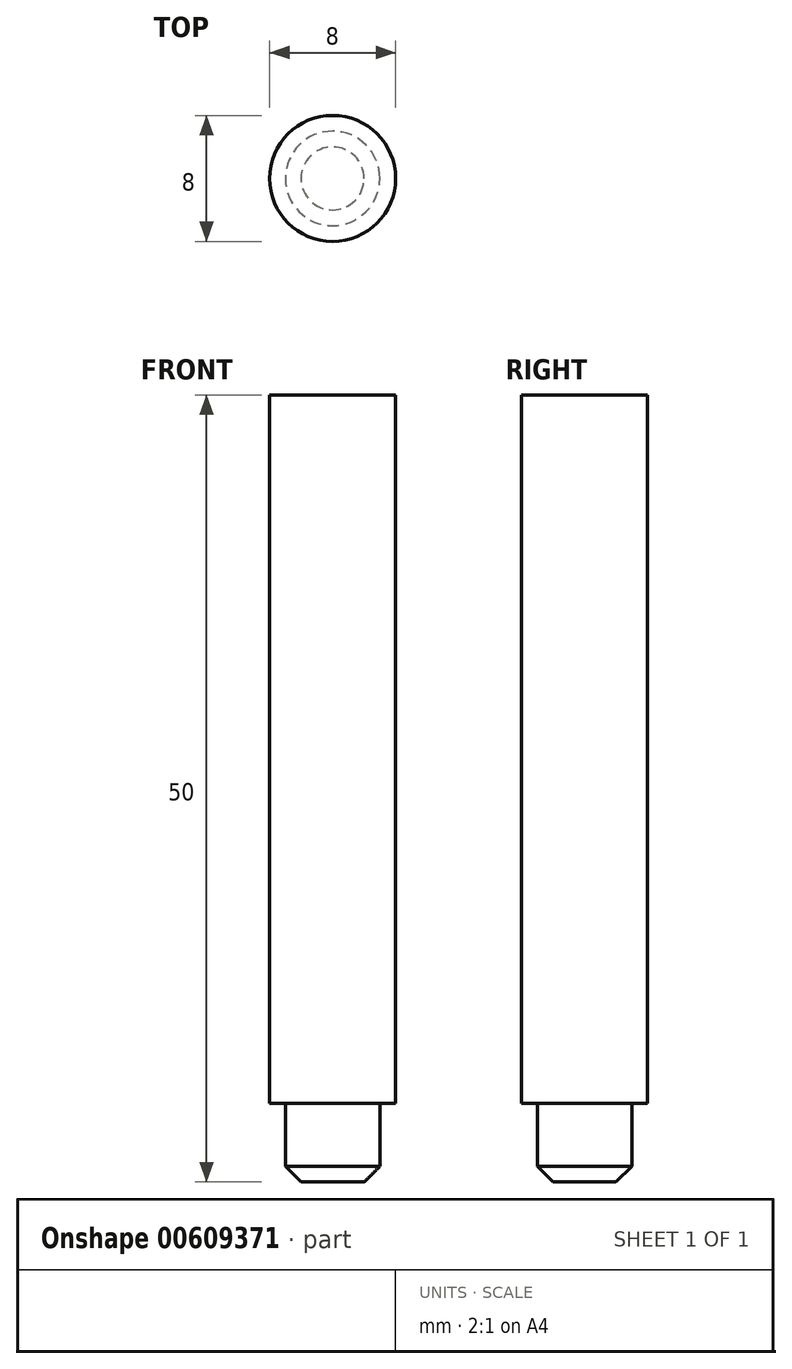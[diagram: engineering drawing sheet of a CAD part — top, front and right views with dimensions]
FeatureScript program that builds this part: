
annotation { "Feature Type Name" : "Feature", "Feature Type Description" : "" }
export const myFeature = defineFeature(function(context is Context, id is Id, definition is map)
    precondition{}
    {
        {
            var Q0;
            Q0=qCreatedBy(makeId("Top.planeOp"),FACE);
            var sketch = newSketch(context, id + "F0", { "sketchPlane" : qUnion([Q0])});
            skCircle(sketch, "E0", {"center": v(0, 0) * mm, "radius": 4 * mm});
            skCircle(sketch, "E1", {"center": v(0, 0) * mm, "radius": 3 * mm});
            skSolve(sketch);
        }
        {
            var Q0;
            Q0=makeQuery(id+"F0.imprint","IMPRINT",FACE,{"disambiguationData":[TD([[makeQuery(id+"F0.imprint","IMPRINT",EDGE,{"derivedFrom":sQuery(id+"F0.wireOp",EDGE,"E1")}),1.0]])]});
            var Q1;
            Q1=makeQuery(id+"F0.imprint","IMPRINT",FACE,{"disambiguationData":[TD([[makeQuery(id+"F0.imprint","IMPRINT",EDGE,{"derivedFrom":sQuery(id+"F0.wireOp",EDGE,"E0")}),1.0]])]});
            extrude(context, id + "F1", {"entities" : qUnion([Q0, Q1]), "oppositeDirection" : true, "depth" : 35 * mm, "offsetDistance" : 25 * mm, "hasSecondDirection" : true, "secondDirectionOppositeDirection" : false, "secondDirectionDepth" : 10 * mm});
        }
        {
            var Q0;
            Q0=makeQuery(id+"F0.imprint","IMPRINT",FACE,{"disambiguationData":[TD([[makeQuery(id+"F0.imprint","IMPRINT",EDGE,{"derivedFrom":sQuery(id+"F0.wireOp",EDGE,"E1")}),1.0]])]});
            extrude(context, id + "F2", {"entities" : qUnion([Q0]), "operationType" : NewBodyOperationType.ADD, "oppositeDirection" : true, "depth" : 40 * mm, "offsetDistance" : 25 * mm});
        }
        {
            var Q0;
            Q0=makeQuery(id+"F2.opExtrude","CAP_EDGE",EDGE,{"disambiguationData":[OSD([sQuery(id+"F0.wireOp",EDGE,"E1")])],"isStart":false});
            chamfer(context, id + "F3", {"entities" : qUnion([Q0]), "width" : 1 * mm, "tangentPropagation" : true});
        }
    });
